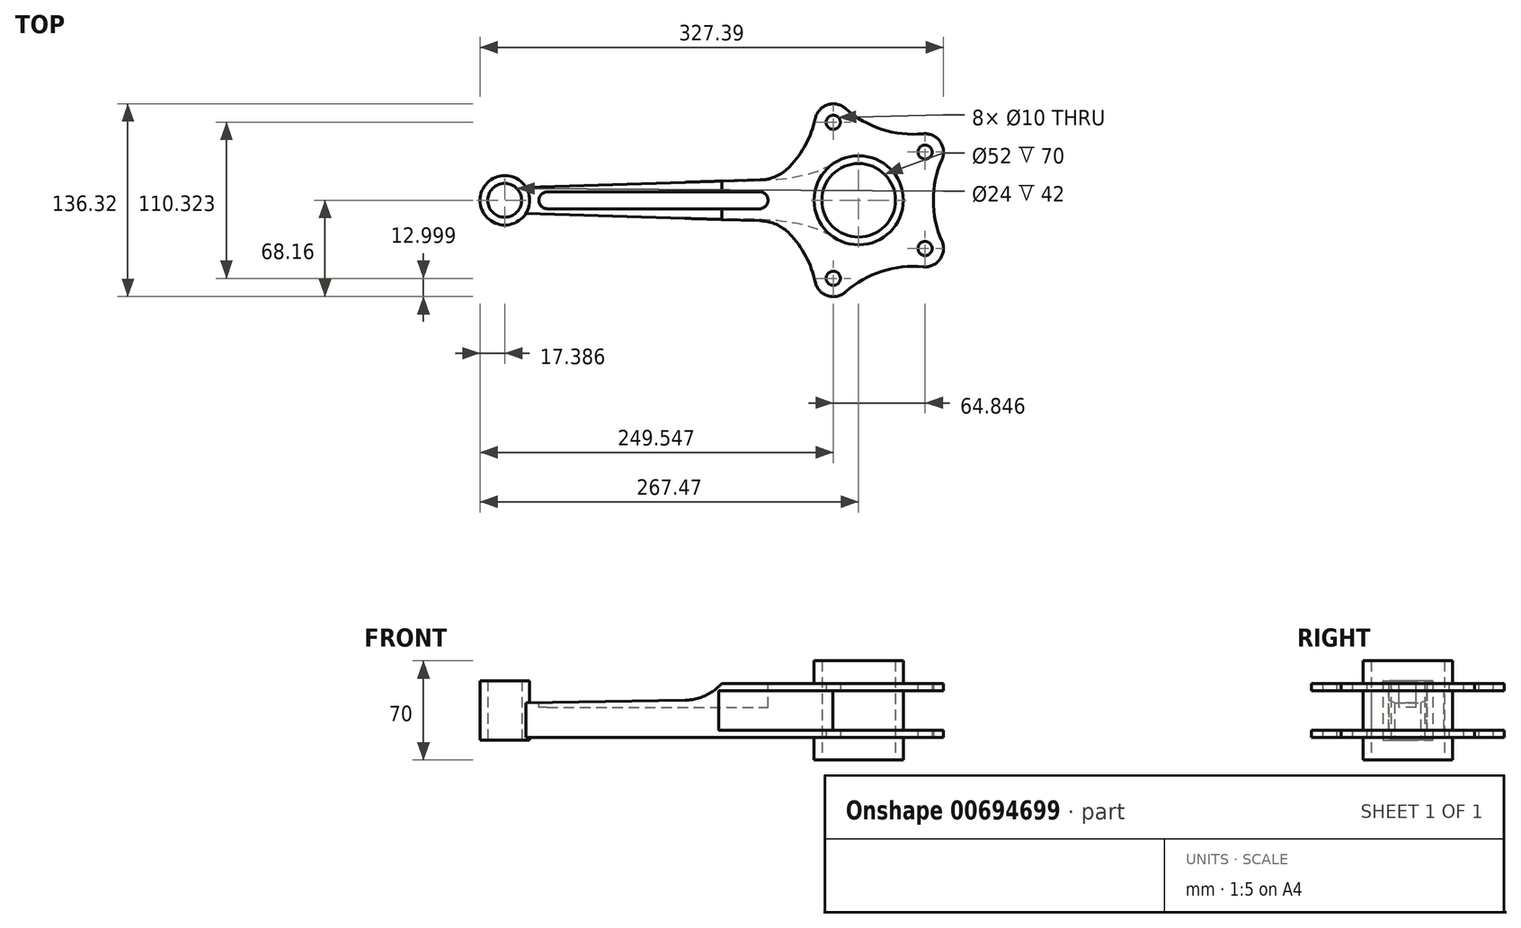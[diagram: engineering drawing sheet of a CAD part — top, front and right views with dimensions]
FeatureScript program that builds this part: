
annotation { "Feature Type Name" : "Feature", "Feature Type Description" : "" }
export const myFeature = defineFeature(function(context is Context, id is Id, definition is map)
    precondition{}
    {
        {
            var Q0;
            Q0=qCreatedBy(makeId("Top.planeOp"),FACE);
            var sketch = newSketch(context, id + "F0", { "sketchPlane" : qUnion([Q0])});
            skArc(sketch, "E0", {"start": v(-242.06, 9) * mm, "mid": v(-262, 0) * mm, "end": v(-242.06, -9) * mm});
            skLineSegment(sketch, "E1", {"start": v(-250, 0) * mm, "end": v(-238, 0) * mm, "construction": true});
            skPoint(sketch, "E2.orphan", {"position": v(0, 9) * mm});
            skPoint(sketch, "E3.orphan", {"position": v(0, -9) * mm});
            skPoint(sketch, "E4.orphan", {"position": v(-178, 9) * mm});
            skPoint(sketch, "E5.orphan", {"position": v(-178, -9) * mm});
            skLineSegment(sketch, "E6", {"start": v(0, 0) * mm, "end": v(58, 0) * mm, "construction": true});
            skCircle(sketch, "E7.cCircle", {"center": v(0, 0) * mm, "radius": 58 * mm, "construction": true});
            skLineSegment(sketch, "E7.1", {"start": v(58, -42.14) * mm, "end": v(56.82, -42.52) * mm});
            skPoint(sketch, "E7.0.midPoint", {"position": v(58, 0) * mm});
            skLineSegment(sketch, "E8", {"start": v(-22.15, 68.18) * mm, "end": v(0, 0) * mm, "construction": true});
            skLineSegment(sketch, "E9", {"start": v(-22.15, -68.18) * mm, "end": v(0, 0) * mm, "construction": true});
            skArc(sketch, "E10", {"start": v(45.64, -47.03) * mm, "mid": v(57.44, -41.73) * mm, "end": v(58.83, -28.88) * mm});
            skArc(sketch, "E11", {"start": v(58.83, 28.88) * mm, "mid": v(57.44, 41.73) * mm, "end": v(45.64, 47.03) * mm});
            skArc(sketch, "E12", {"start": v(-9.28, 64.88) * mm, "mid": v(-21.94, 67.53) * mm, "end": v(-30.62, 57.94) * mm});
            skArc(sketch, "E13", {"start": v(-30.62, -57.94) * mm, "mid": v(-21.94, -67.53) * mm, "end": v(-9.28, -64.88) * mm});
            skArc(sketch, "E14", {"start": v(58.83, 28.88) * mm, "mid": v(52.79, 0) * mm, "end": v(58.83, -28.88) * mm});
            skLineSegment(sketch, "E15.trimOffspring", {"start": v(58, -40.9) * mm, "end": v(58, -42.14) * mm});
            skArc(sketch, "E16.1.0", {"start": v(45.64, -47.03) * mm, "mid": v(16.31, -50.2) * mm, "end": v(-9.28, -64.88) * mm});
            skArc(sketch, "E16.2.0", {"start": v(-30.62, -57.94) * mm, "mid": v(-40.84, -33.72) * mm, "end": v(-59.08, -14.78) * mm});
            skPoint(sketch, "E17.orphan", {"position": v(-64.57, -11.22) * mm});
            skArc(sketch, "E18.MirrorCS", {"start": v(45.64, 47.03) * mm, "mid": v(16.31, 50.2) * mm, "end": v(-9.28, 64.88) * mm});
            skArc(sketch, "E19.MirrorCS", {"start": v(-30.62, 57.94) * mm, "mid": v(-40.84, 33.72) * mm, "end": v(-59.08, 14.78) * mm});
            skPoint(sketch, "E20.orphan", {"position": v(-71.7, 0) * mm});
            skCircle(sketch, "E21", {"center": v(-17.92, -55.16) * mm, "radius": 5 * mm});
            skCircle(sketch, "E22", {"center": v(46.92, -34.1) * mm, "radius": 5 * mm});
            skCircle(sketch, "E23", {"center": v(46.92, 34.1) * mm, "radius": 5 * mm});
            skCircle(sketch, "E24", {"center": v(-17.92, 55.16) * mm, "radius": 5 * mm});
            skLineSegment(sketch, "E25", {"start": v(-242.06, 9) * mm, "end": v(-59.08, 14.78) * mm});
            skLineSegment(sketch, "E26.MirrorCS", {"start": v(-242.06, -9) * mm, "end": v(-59.08, -14.78) * mm});
            skPoint(sketch, "E27.trimOffspring.end.orphan", {"position": v(-68.65, 9) * mm});
            skPoint(sketch, "E28.trimOffspring.end.orphan", {"position": v(-68.65, -9) * mm});
            skLineSegment(sketch, "E29.trimOffspring", {"start": v(-58, 0) * mm, "end": v(0, 0) * mm, "construction": true});
            skLineSegment(sketch, "E30", {"start": v(0, 0) * mm, "end": v(46.92, 34.1) * mm, "construction": true});
            skLineSegment(sketch, "E31", {"start": v(0, 0) * mm, "end": v(46.92, -34.1) * mm, "construction": true});
            skSolve(sketch);
        }
        {
            var Q0;
            Q0=makeQuery(id+"F0.imprint","IMPRINT",FACE,{"disambiguationData":[TD([[makeQuery(id+"F0.imprint","IMPRINT",EDGE,{"derivedFrom":sQuery(id+"F0.wireOp",EDGE,"E0")}),1.0]])]});
            extrude(context, id + "F1", {"entities" : qUnion([Q0]), "depth" : (28 + 10) * mm, "offsetDistance" : 25 * mm, "symmetric" : true});
        }
        {
            var Q0;
            Q0=makeQuery(id+"F1.opExtrude","SWEPT_EDGE",EDGE,{"disambiguationData":[OSD([sQuery(id+"F0.wireOp",EDGE,"E16.2.0"),sQuery(id+"F0.wireOp",EDGE,"E26.MirrorCS")])]});
            var Q1;
            Q1=makeQuery(id+"F1.opExtrude","SWEPT_EDGE",EDGE,{"disambiguationData":[OSD([sQuery(id+"F0.wireOp",EDGE,"E19.MirrorCS"),sQuery(id+"F0.wireOp",EDGE,"E25")])]});
            fillet(context, id + "F2", {"entities" : qUnion([Q0, Q1]), "radius" : 30 * mm, "tangentPropagation" : true, "allowEdgeOverflow" : false});
        }
        {
            var Q0;
            Q0=qCreatedBy(makeId("Front.planeOp"),FACE);
            var sketch = newSketch(context, id + "F3", { "sketchPlane" : qUnion([Q0])});
            skLineSegment(sketch, "E32", {"start": v(-263.6, 5.18) * mm, "end": v(-237.18, 5.18) * mm});
            skLineSegment(sketch, "E33", {"start": v(-237.18, 5.18) * mm, "end": v(-122.66, 7.14) * mm});
            skArc(sketch, "E34", {"start": v(-122.66, 7.14) * mm, "mid": v(-107.33, 10.9) * mm, "end": v(-95.12, 20.89) * mm});
            skLineSegment(sketch, "E35", {"start": v(-263.6, 5.18) * mm, "end": v(-263.6, 30.47) * mm});
            skPoint(sketch, "E36.end.orphan", {"position": v(-98.3, 15.81) * mm});
            skLineSegment(sketch, "E37", {"start": v(-263.6, 30.47) * mm, "end": v(-99.95, 36.16) * mm});
            skLineSegment(sketch, "E38", {"start": v(-95.12, 20.89) * mm, "end": v(-99.95, 36.16) * mm});
            skPoint(sketch, "E39.end.orphan", {"position": v(-99.95, 15.81) * mm});
            skSolve(sketch);
        }
        {
            var Q0;
            Q0=makeQuery(id+"F3.imprint","IMPRINT",FACE,{"disambiguationData":[TD([[makeQuery(id+"F3.imprint","IMPRINT",EDGE,{"derivedFrom":sQuery(id+"F3.wireOp",EDGE,"E32")}),1.0]])]});
            extrude(context, id + "F4", {"entities" : qUnion([Q0]), "operationType" : NewBodyOperationType.REMOVE, "endBound" : BoundingType.THROUGH_ALL, "depth" : 25 * mm, "offsetDistance" : 25 * mm, "hasSecondDirection" : true, "secondDirectionBound" : BoundingType.THROUGH_ALL, "secondDirectionOppositeDirection" : true, "secondDirectionDepth" : 25 * mm});
        }
        {
            var Q0;
            Q0=makeQuery(id+"F1.opExtrude","CAP_FACE",FACE,{"disambiguationData":[OSD([sQuery(id+"F0.wireOp",EDGE,"E0"),sQuery(id+"F0.wireOp",EDGE,"E10"),sQuery(id+"F0.wireOp",EDGE,"E11"),sQuery(id+"F0.wireOp",EDGE,"E12"),sQuery(id+"F0.wireOp",EDGE,"E13"),sQuery(id+"F0.wireOp",EDGE,"E14"),sQuery(id+"F0.wireOp",EDGE,"E16.1.0"),sQuery(id+"F0.wireOp",EDGE,"E16.2.0"),sQuery(id+"F0.wireOp",EDGE,"E18.MirrorCS"),sQuery(id+"F0.wireOp",EDGE,"E19.MirrorCS"),sQuery(id+"F0.wireOp",EDGE,"E21"),sQuery(id+"F0.wireOp",EDGE,"E22"),sQuery(id+"F0.wireOp",EDGE,"E23"),sQuery(id+"F0.wireOp",EDGE,"E24"),sQuery(id+"F0.wireOp",EDGE,"E25"),sQuery(id+"F0.wireOp",EDGE,"E26.MirrorCS")])],"isStart":false});
            var sketch = newSketch(context, id + "F5", { "sketchPlane" : qUnion([Q0])});
            skLineSegment(sketch, "E40", {"start": v(-250, 0) * mm, "end": v(-250, 43.21) * mm, "construction": true});
            skLineSegment(sketch, "E41.0", {"start": v(-220, -18.1) * mm, "end": v(-220, 43.21) * mm, "construction": true});
            skLineSegment(sketch, "E42.0", {"start": v(-70, -29.5) * mm, "end": v(-70, 43.21) * mm, "construction": true});
            skArc(sketch, "E43", {"start": v(-70, -6) * mm, "mid": v(-64, 0) * mm, "end": v(-70, 6) * mm});
            skArc(sketch, "E44", {"start": v(-220, 6) * mm, "mid": v(-226, 0) * mm, "end": v(-220, -6) * mm});
            skLineSegment(sketch, "E45", {"start": v(-220, 6) * mm, "end": v(-70, 6) * mm});
            skLineSegment(sketch, "E46", {"start": v(-220, -6) * mm, "end": v(-70, -6) * mm});
            skSolve(sketch);
        }
        {
            var Q0;
            {var subQ0=sQuery(id+"F5.wireOp",EDGE,"E44");Q0=makeQuery(id+"F5.imprint","IMPRINT",FACE,{"disambiguationData":[TD([[makeQuery(id+"F5.imprint","IMPRINT",EDGE,{"derivedFrom":subQ0}),1.0]])]});}
            var Q1;
            {var subQ0=sQuery(id+"F5.wireOp",EDGE,"E43");Q1=makeQuery(id+"F5.imprint","IMPRINT",FACE,{"disambiguationData":[TD([[makeQuery(id+"F5.imprint","IMPRINT",EDGE,{"derivedFrom":subQ0}),1.0]])]});}
            extrude(context, id + "F6", {"entities" : qUnion([Q0, Q1]), "operationType" : NewBodyOperationType.REMOVE, "oppositeDirection" : true, "depth" : 17 * mm, "offsetDistance" : 25 * mm});
        }
        {
            var Q0;
            Q0=qCreatedBy(makeId("Top.planeOp"),FACE);
            var sketch = newSketch(context, id + "F7", { "sketchPlane" : qUnion([Q0])});
            skCircle(sketch, "E47", {"center": v(-249.97, 0) * mm, "radius": 17.5 * mm});
            skSolve(sketch);
        }
        {
            var Q0;
            Q0 = qSketchRegion(id + "F7", true);
            extrude(context, id + "F8", {"entities" : qUnion([Q0]), "operationType" : NewBodyOperationType.ADD, "depth" : 42 * mm, "offsetDistance" : 25 * mm, "symmetric" : true});
        }
        {
            var Q0;
            Q0=qCreatedBy(makeId("Top.planeOp"),FACE);
            var sketch = newSketch(context, id + "F9", { "sketchPlane" : qUnion([Q0])});
            skCircle(sketch, "E48", {"center": v(0, 0) * mm, "radius": 31.5 * mm});
            skSolve(sketch);
        }
        {
            var Q0;
            Q0 = qSketchRegion(id + "F9", true);
            extrude(context, id + "F10", {"entities" : qUnion([Q0]), "operationType" : NewBodyOperationType.ADD, "depth" : 70 * mm, "offsetDistance" : 25 * mm, "symmetric" : true});
        }
        {
            var Q0;
            Q0=qCreatedBy(makeId("Top.planeOp"),FACE);
            var sketch = newSketch(context, id + "F11", { "sketchPlane" : qUnion([Q0])});
            skCircle(sketch, "E49", {"center": v(0, 0) * mm, "radius": 26 * mm});
            skCircle(sketch, "E50", {"center": v(-250.08, 0) * mm, "radius": 12 * mm});
            skSolve(sketch);
        }
        {
            var Q0;
            Q0 = qSketchRegion(id + "F11", true);
            extrude(context, id + "F12", {"entities" : qUnion([Q0]), "operationType" : NewBodyOperationType.REMOVE, "endBound" : BoundingType.THROUGH_ALL, "depth" : 25 * mm, "offsetDistance" : 25 * mm, "hasSecondDirection" : true, "secondDirectionBound" : BoundingType.THROUGH_ALL, "secondDirectionOppositeDirection" : true, "secondDirectionDepth" : 25 * mm});
        }
        {
            var Q0;
            Q0=qCreatedBy(makeId("Top.planeOp"),FACE);
            var sketch = newSketch(context, id + "F13", { "sketchPlane" : qUnion([Q0])});
            skArc(sketch, "E51", {"start": v(-18.3, -25.64) * mm, "mid": v(31.5, 0) * mm, "end": v(-18.3, 25.64) * mm});
            skFitSpline(sketch, "E52", {"points": [v(-18.3, 25.64) * mm, v(-47.73, 15.74) * mm, v(-99.07, 13.39) * mm], "startDerivative": vector(-63.18, -36.03) * mm, "endDerivative": vector(-115.12, 0.93) * mm});
            skFitSpline(sketch, "E53.MirrorCS", {"points": [v(-18.3, -25.64) * mm, v(-47.73, -15.74) * mm, v(-99.07, -13.39) * mm], "startDerivative": vector(-63.18, 36.03) * mm, "endDerivative": vector(-115.12, -0.93) * mm});
            skLineSegment(sketch, "E54", {"start": v(-99.07, 13.39) * mm, "end": v(-91, 91.08) * mm});
            skLineSegment(sketch, "E55", {"start": v(-91, 91.08) * mm, "end": v(95.2, 50.92) * mm});
            skLineSegment(sketch, "E56", {"start": v(95.2, 50.92) * mm, "end": v(80.9, -76.39) * mm});
            skLineSegment(sketch, "E57", {"start": v(80.9, -76.39) * mm, "end": v(-70.24, -76.39) * mm});
            skLineSegment(sketch, "E58", {"start": v(-70.24, -76.39) * mm, "end": v(-99.07, -13.39) * mm});
            skSolve(sketch);
        }
        {
            var Q0;
            Q0=makeQuery(id+"F13.imprint","IMPRINT",FACE,{"disambiguationData":[TD([[makeQuery(id+"F13.imprint","IMPRINT",EDGE,{"derivedFrom":sQuery(id+"F13.wireOp",EDGE,"E51")}),-1.0]])]});
            extrude(context, id + "F14", {"entities" : qUnion([Q0]), "operationType" : NewBodyOperationType.REMOVE, "oppositeDirection" : true, "depth" : 28 * mm, "offsetDistance" : 25 * mm, "symmetric" : true});
        }
    });
